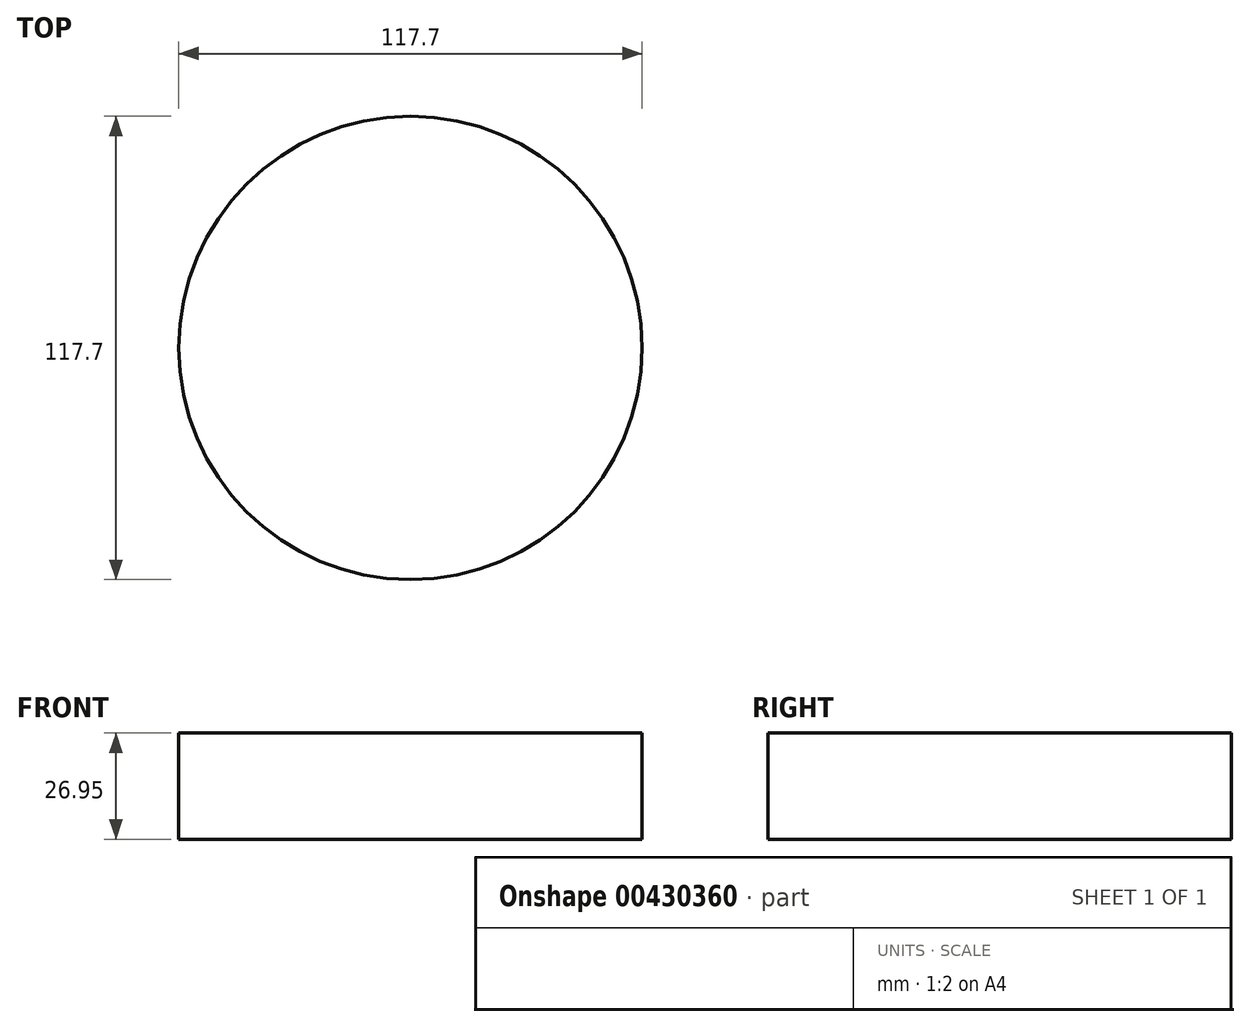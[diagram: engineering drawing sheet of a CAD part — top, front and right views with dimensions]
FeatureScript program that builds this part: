
annotation { "Feature Type Name" : "Feature", "Feature Type Description" : "" }
export const myFeature = defineFeature(function(context is Context, id is Id, definition is map)
    precondition{}
    {
        {
            var Q0;
            Q0=qCreatedBy(makeId("Top.planeOp"),FACE);
            var sketch = newSketch(context, id + "F0", { "sketchPlane" : qUnion([Q0])});
            skCircle(sketch, "E0", {"center": v(40.17, -210.13) * mm, "radius": 58.85 * mm});
            skSolve(sketch);
        }
        {
            var Q0;
            Q0=makeQuery(id+"F0.imprint","IMPRINT",FACE,{"disambiguationData":[TD([[makeQuery(id+"F0.imprint","IMPRINT",EDGE,{"derivedFrom":sQuery(id+"F0.wireOp",EDGE,"E0")}),1.0]])]});
            extrude(context, id + "F1", {"entities" : qUnion([Q0]), "depth" : 26.95 * mm});
        }
    });
